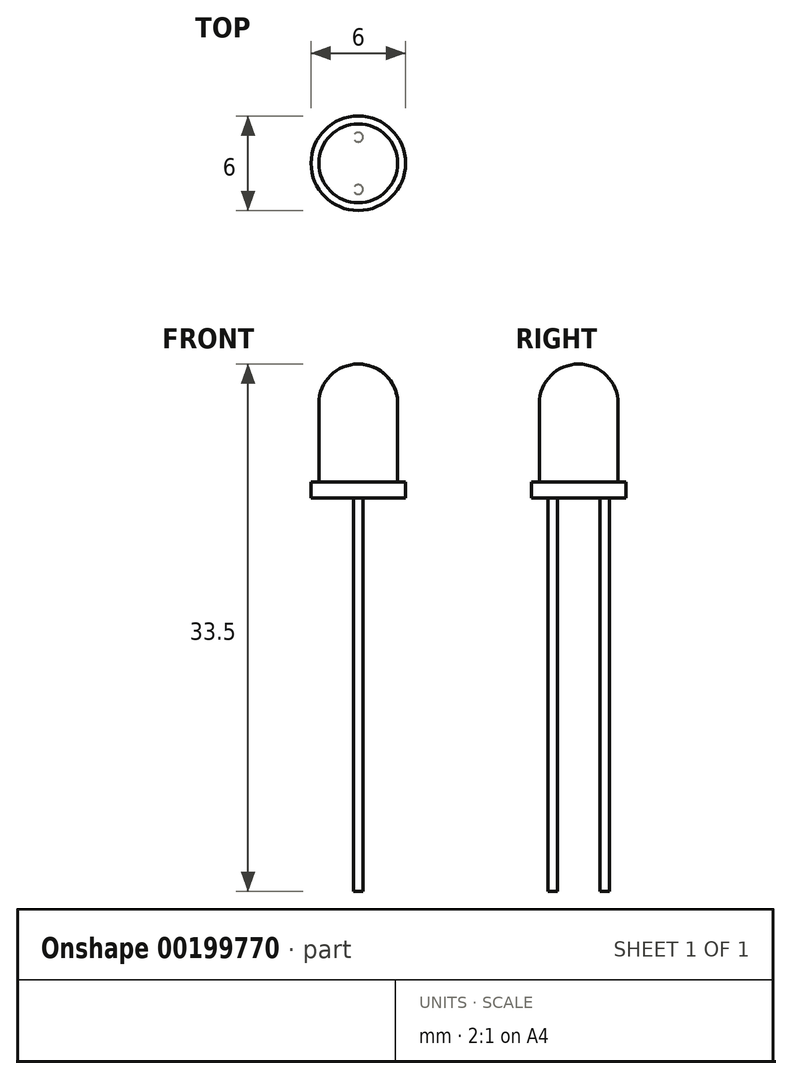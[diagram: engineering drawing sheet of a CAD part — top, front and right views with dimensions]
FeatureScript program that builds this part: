
annotation { "Feature Type Name" : "Feature", "Feature Type Description" : "" }
export const myFeature = defineFeature(function(context is Context, id is Id, definition is map)
    precondition{}
    {
        {
            var Q0;
            Q0=qCreatedBy(makeId("Front.planeOp"),FACE);
            var sketch = newSketch(context, id + "F0", { "sketchPlane" : qUnion([Q0])});
            skLineSegment(sketch, "E0", {"start": v(0, 0) * mm, "end": v(0, 8.5) * mm});
            skLineSegment(sketch, "E1", {"start": v(0, 0) * mm, "end": v(3, 0) * mm});
            skLineSegment(sketch, "E2", {"start": v(3, 0) * mm, "end": v(3, 1) * mm});
            skLineSegment(sketch, "E3", {"start": v(3, 1) * mm, "end": v(2.5, 1) * mm});
            skLineSegment(sketch, "E4", {"start": v(2.5, 1) * mm, "end": v(2.5, 6) * mm});
            skArc(sketch, "E5", {"start": v(2.5, 6) * mm, "mid": v(1.77, 7.77) * mm, "end": v(0, 8.5) * mm});
            skSolve(sketch);
        }
        {
            var Q0;
            Q0=qCreatedBy(makeId("Right.planeOp"),FACE);
            var sketch = newSketch(context, id + "F1", { "sketchPlane" : qUnion([Q0])});
            skLineSegment(sketch, "E6", {"start": v(0, 0) * mm, "end": v(0, 11.17) * mm});
            skSolve(sketch);
        }
        {
            var Q0;
            Q0=makeQuery(id+"F0.imprint","IMPRINT",FACE,{"disambiguationData":[TD([[makeQuery(id+"F0.imprint","IMPRINT",EDGE,{"derivedFrom":sQuery(id+"F0.wireOp",EDGE,"E0")}),-1.0]])]});
            var Q1;
            Q1=sQuery(id+"F1.wireOp",EDGE,"E6");
            revolve(context, id + "F2", {"entities" : qUnion([Q0]), "axis" : qUnion([Q1]), "revolveType" : RevolveType.FULL});
        }
        {
            var Q0;
            Q0=makeQuery(id+"F2.opRevolve","SWEPT_FACE",FACE,{"disambiguationData":[OSD([sQuery(id+"F0.wireOp",EDGE,"E1")])]});
            var sketch = newSketch(context, id + "F3", { "sketchPlane" : qUnion([Q0])});
            skCircle(sketch, "E7", {"center": v(0, -1.66) * mm, "radius": 0.3 * mm});
            skCircle(sketch, "E8", {"center": v(0, 1.66) * mm, "radius": 0.3 * mm});
            skLineSegment(sketch, "E9", {"start": v(0, 1.66) * mm, "end": v(0, 0) * mm});
            skLineSegment(sketch, "E10", {"start": v(0, 0) * mm, "end": v(0, -1.66) * mm});
            skSolve(sketch);
        }
        {
            var Q0;
            Q0=makeQuery(id+"F3.imprint","IMPRINT",FACE,{"disambiguationData":[TD([[makeQuery(id+"F3.imprint","IMPRINT",EDGE,{"derivedFrom":sQuery(id+"F3.wireOp",EDGE,"E7")}),1.0]])]});
            var Q1;
            Q1=makeQuery(id+"F3.imprint","IMPRINT",FACE,{"disambiguationData":[TD([[makeQuery(id+"F3.imprint","IMPRINT",EDGE,{"derivedFrom":sQuery(id+"F3.wireOp",EDGE,"E8")}),1.0]])]});
            extrude(context, id + "F4", {"entities" : qUnion([Q0, Q1]), "operationType" : NewBodyOperationType.ADD, "depth" : 25 * mm});
        }
    });
